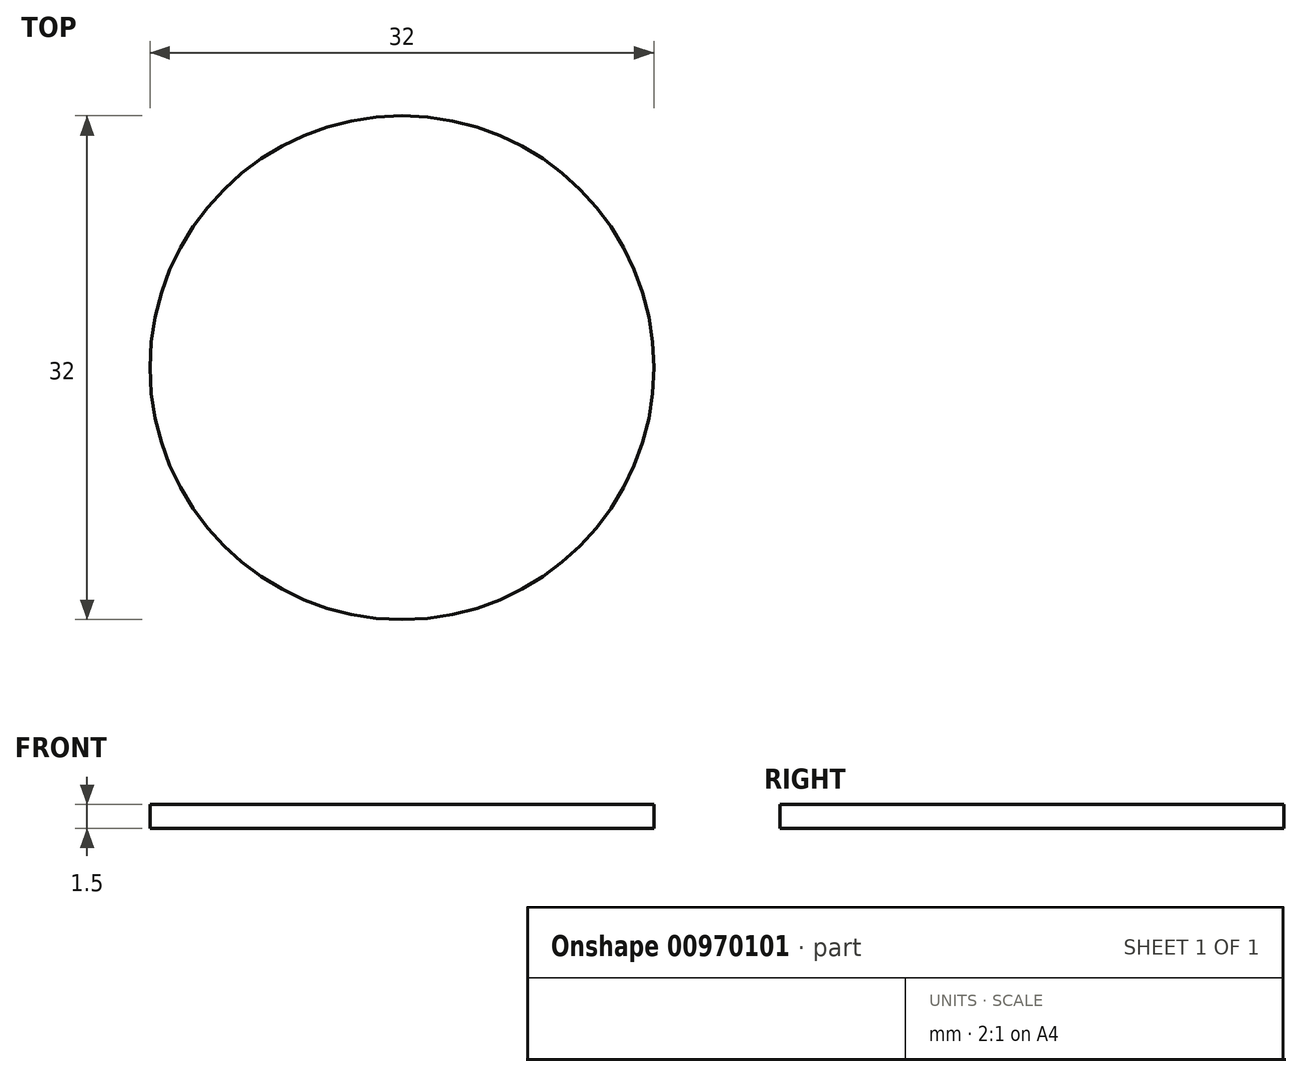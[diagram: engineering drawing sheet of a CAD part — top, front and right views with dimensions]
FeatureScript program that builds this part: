
annotation { "Feature Type Name" : "Feature", "Feature Type Description" : "" }
export const myFeature = defineFeature(function(context is Context, id is Id, definition is map)
    precondition{}
    {
        {
            var Q0;
            Q0=qCreatedBy(makeId("Top.planeOp"),FACE);
            var sketch = newSketch(context, id + "F0", { "sketchPlane" : qUnion([Q0])});
            skCircle(sketch, "E0", {"center": v(0, 0) * mm, "radius": 16 * mm});
            skSolve(sketch);
        }
        {
            var Q0;
            Q0 = qSketchRegion(id + "F0", true);
            var Q1;
            Q1=makeQuery(id+"F0.imprint","IMPRINT",FACE,{"disambiguationData":[TD([[makeQuery(id+"F0.imprint","IMPRINT",EDGE,{"derivedFrom":sQuery(id+"F0.wireOp",EDGE,"E0")}),1.0]])]});
            extrude(context, id + "F1", {"entities" : qUnion([Q0, Q1]), "depth" : 1.5 * mm, "offsetDistance" : 25 * mm});
        }
    });
